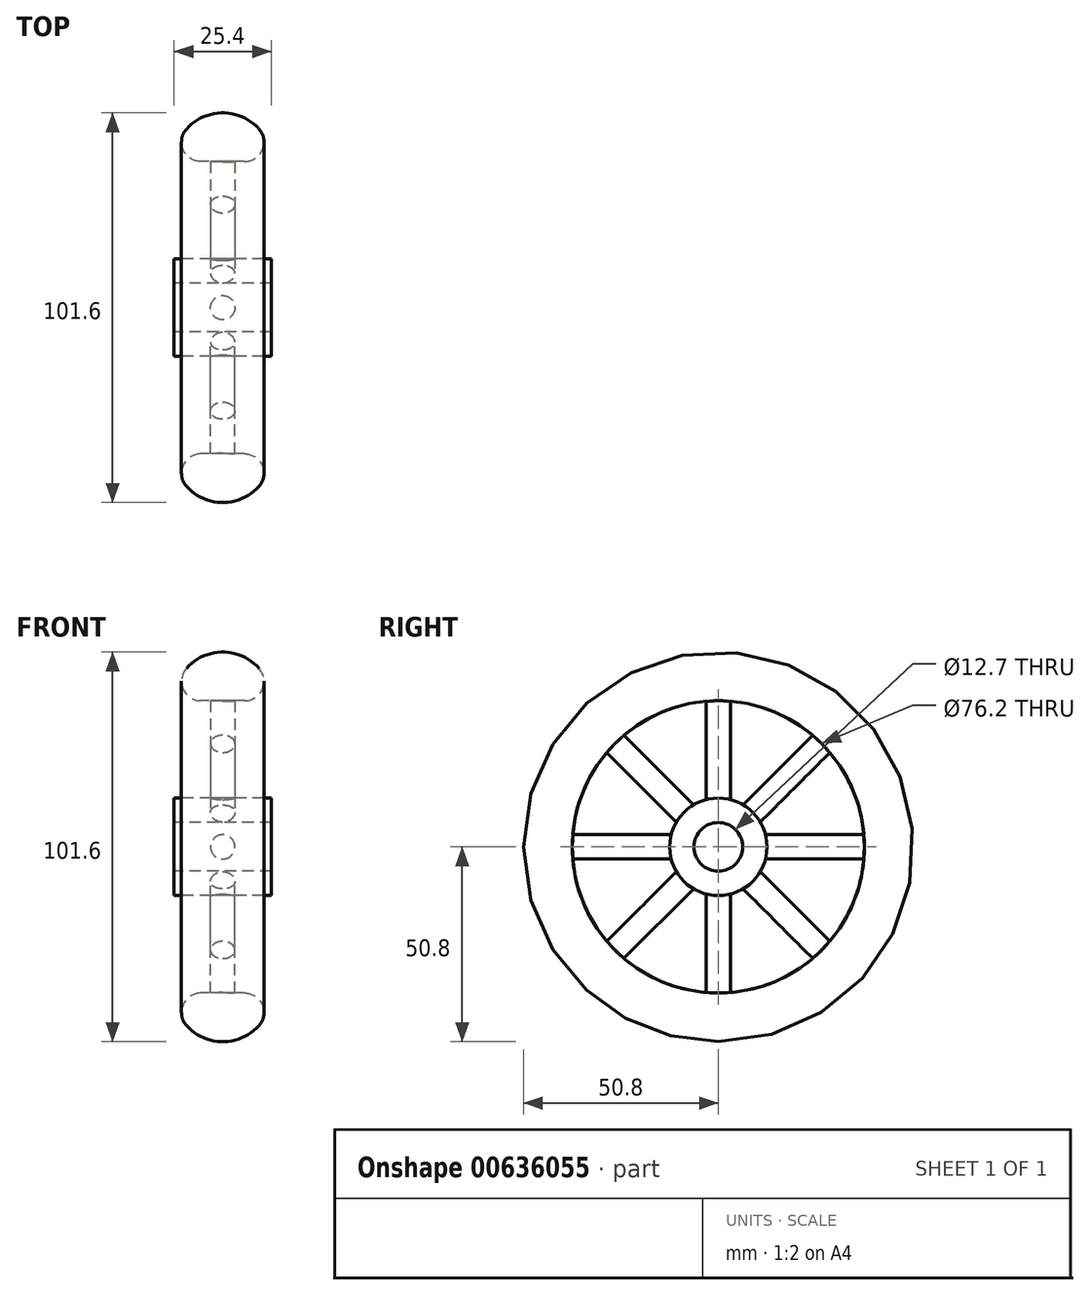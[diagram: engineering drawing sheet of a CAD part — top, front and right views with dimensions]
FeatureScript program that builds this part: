
annotation { "Feature Type Name" : "Feature", "Feature Type Description" : "" }
export const myFeature = defineFeature(function(context is Context, id is Id, definition is map)
    precondition{}
    {
        {
            var Q0;
            Q0=qCreatedBy(makeId("Right.planeOp"),FACE);
            var sketch = newSketch(context, id + "F0", { "sketchPlane" : qUnion([Q0])});
            skCircle(sketch, "E0", {"center": v(0, 0) * mm, "radius": 50.8 * mm});
            skCircle(sketch, "E1", {"center": v(0, 0) * mm, "radius": 38.1 * mm});
            skCircle(sketch, "E2", {"center": v(0, 0) * mm, "radius": 6.35 * mm});
            skCircle(sketch, "E3", {"center": v(0, 0) * mm, "radius": 12.7 * mm});
            skLineSegment(sketch, "E4.0", {"start": v(-3.18, 12.3) * mm, "end": v(-3.18, 37.97) * mm});
            skLineSegment(sketch, "E5.0", {"start": v(3.17, 12.3) * mm, "end": v(3.17, 37.97) * mm});
            skLineSegment(sketch, "E6.1.0", {"start": v(-10.94, 6.45) * mm, "end": v(-29.1, 24.6) * mm});
            skLineSegment(sketch, "E6.1.1", {"start": v(-6.45, 10.94) * mm, "end": v(-24.6, 29.1) * mm});
            skLineSegment(sketch, "E6.2.0", {"start": v(-12.3, -3.18) * mm, "end": v(-37.97, -3.17) * mm});
            skLineSegment(sketch, "E6.2.1", {"start": v(-12.3, 3.17) * mm, "end": v(-37.97, 3.18) * mm});
            skLineSegment(sketch, "E6.3.0", {"start": v(-6.45, -10.94) * mm, "end": v(-24.6, -29.1) * mm});
            skLineSegment(sketch, "E6.3.1", {"start": v(-10.94, -6.45) * mm, "end": v(-29.1, -24.6) * mm});
            skLineSegment(sketch, "E6.4.0", {"start": v(3.18, -12.3) * mm, "end": v(3.17, -37.97) * mm});
            skLineSegment(sketch, "E6.4.1", {"start": v(-3.18, -12.3) * mm, "end": v(-3.18, -37.97) * mm});
            skLineSegment(sketch, "E6.5.0", {"start": v(10.94, -6.45) * mm, "end": v(29.1, -24.6) * mm});
            skLineSegment(sketch, "E6.5.1", {"start": v(6.45, -10.94) * mm, "end": v(24.6, -29.1) * mm});
            skLineSegment(sketch, "E6.6.0", {"start": v(12.3, 3.18) * mm, "end": v(37.97, 3.17) * mm});
            skLineSegment(sketch, "E6.6.1", {"start": v(12.3, -3.18) * mm, "end": v(37.97, -3.18) * mm});
            skLineSegment(sketch, "E6.7.0", {"start": v(6.45, 10.94) * mm, "end": v(24.6, 29.1) * mm});
            skLineSegment(sketch, "E6.7.1", {"start": v(10.94, 6.45) * mm, "end": v(29.1, 24.6) * mm});
            skSolve(sketch);
        }
        {
            var Q0;
            Q0=makeQuery(id+"F0.imprint","IMPRINT",FACE,{"disambiguationData":[TD([[makeQuery(id+"F0.imprint","IMPRINT",EDGE,{"derivedFrom":sQuery(id+"F0.wireOp",EDGE,"E0")}),1.0]])]});
            extrude(context, id + "F1", {"entities" : qUnion([Q0]), "endBound" : BoundingType.SYMMETRIC, "depth" : 25.4 * mm, "offsetDistance" : 25.4 * mm});
        }
        {
            var Q0;
            Q0=makeQuery(id+"F0.imprint","IMPRINT",FACE,{"disambiguationData":[TD([[makeQuery(id+"F0.imprint","IMPRINT",EDGE,{"derivedFrom":sQuery(id+"F0.wireOp",EDGE,"E2")}),-1.0]])]});
            extrude(context, id + "F2", {"entities" : qUnion([Q0]), "endBound" : BoundingType.SYMMETRIC, "depth" : 25.4 * mm, "offsetDistance" : 25.4 * mm});
        }
        {
            var Q0;
            {var subQ0=sQuery(id+"F0.wireOp",EDGE,"E6.1.0");Q0=makeQuery(id+"F0.imprint","IMPRINT",FACE,{"disambiguationData":[TD([[makeQuery(id+"F0.imprint","IMPRINT",EDGE,{"derivedFrom":subQ0}),-1.0]])]});}
            var Q1;
            {var subQ0=sQuery(id+"F0.wireOp",EDGE,"E4.0");Q1=makeQuery(id+"F0.imprint","IMPRINT",FACE,{"disambiguationData":[TD([[makeQuery(id+"F0.imprint","IMPRINT",EDGE,{"derivedFrom":subQ0}),-1.0]])]});}
            var Q2;
            {var subQ0=sQuery(id+"F0.wireOp",EDGE,"E6.7.0");Q2=makeQuery(id+"F0.imprint","IMPRINT",FACE,{"disambiguationData":[TD([[makeQuery(id+"F0.imprint","IMPRINT",EDGE,{"derivedFrom":subQ0}),-1.0]])]});}
            var Q3;
            {var subQ0=sQuery(id+"F0.wireOp",EDGE,"E6.6.0");Q3=makeQuery(id+"F0.imprint","IMPRINT",FACE,{"disambiguationData":[TD([[makeQuery(id+"F0.imprint","IMPRINT",EDGE,{"derivedFrom":subQ0}),-1.0]])]});}
            var Q4;
            {var subQ0=sQuery(id+"F0.wireOp",EDGE,"E6.2.0");Q4=makeQuery(id+"F0.imprint","IMPRINT",FACE,{"disambiguationData":[TD([[makeQuery(id+"F0.imprint","IMPRINT",EDGE,{"derivedFrom":subQ0}),-1.0]])]});}
            var Q5;
            {var subQ0=sQuery(id+"F0.wireOp",EDGE,"E6.3.0");Q5=makeQuery(id+"F0.imprint","IMPRINT",FACE,{"disambiguationData":[TD([[makeQuery(id+"F0.imprint","IMPRINT",EDGE,{"derivedFrom":subQ0}),-1.0]])]});}
            var Q6;
            {var subQ0=sQuery(id+"F0.wireOp",EDGE,"E6.4.0");Q6=makeQuery(id+"F0.imprint","IMPRINT",FACE,{"disambiguationData":[TD([[makeQuery(id+"F0.imprint","IMPRINT",EDGE,{"derivedFrom":subQ0}),-1.0]])]});}
            var Q7;
            {var subQ0=sQuery(id+"F0.wireOp",EDGE,"E6.5.0");Q7=makeQuery(id+"F0.imprint","IMPRINT",FACE,{"disambiguationData":[TD([[makeQuery(id+"F0.imprint","IMPRINT",EDGE,{"derivedFrom":subQ0}),-1.0]])]});}
            extrude(context, id + "F3", {"entities" : qUnion([Q0, Q1, Q2, Q3, Q4, Q5, Q6, Q7]), "endBound" : BoundingType.SYMMETRIC, "depth" : 6.35 * mm, "offsetDistance" : 25.4 * mm});
        }
        {
            var Q0;
            Q0=makeQuery(id+"F1.opExtrude","CAP_EDGE",EDGE,{"disambiguationData":[OSD([sQuery(id+"F0.wireOp",EDGE,"E0")])],"isStart":false});
            var Q1;
            Q1=makeQuery(id+"F1.opExtrude","CAP_EDGE",EDGE,{"disambiguationData":[OSD([sQuery(id+"F0.wireOp",EDGE,"E0")])],"isStart":true});
            fillet(context, id + "F4", {"entities" : qUnion([Q0, Q1]), "radius" : 12.7 * mm, "tangentPropagation" : true, "allowEdgeOverflow" : false});
        }
        {
            var Q0;
            Q0=makeQuery(id+"F4.opFillet","BLEND_EDGE",EDGE,{"blendedFrom":[makeQuery(id+"F1.opExtrude","CAP_EDGE",EDGE,{"disambiguationData":[OSD([sQuery(id+"F0.wireOp",EDGE,"E0")])],"isStart":true}),makeQuery(id+"F1.opExtrude","SWEPT_FACE",FACE,{"disambiguationData":[OSD([sQuery(id+"F0.wireOp",EDGE,"E1")])]})],"blendedInto":[makeQuery(id+"F1.opExtrude","SWEPT_FACE",FACE,{"disambiguationData":[OSD([sQuery(id+"F0.wireOp",EDGE,"E1")])]})]});
            var Q1;
            Q1=makeQuery(id+"F4.opFillet","BLEND_EDGE",EDGE,{"blendedFrom":[makeQuery(id+"F1.opExtrude","CAP_EDGE",EDGE,{"disambiguationData":[OSD([sQuery(id+"F0.wireOp",EDGE,"E0")])],"isStart":false}),makeQuery(id+"F1.opExtrude","SWEPT_FACE",FACE,{"disambiguationData":[OSD([sQuery(id+"F0.wireOp",EDGE,"E1")])]})],"blendedInto":[makeQuery(id+"F1.opExtrude","SWEPT_FACE",FACE,{"disambiguationData":[OSD([sQuery(id+"F0.wireOp",EDGE,"E1")])]})]});
            fillet(context, id + "F5", {"entities" : qUnion([Q0, Q1]), "radius" : 5.08 * mm, "tangentPropagation" : true, "allowEdgeOverflow" : false});
        }
        {
            var Q0;
            Q0=makeQuery(id+"F3.opExtrude","CAP_EDGE",EDGE,{"disambiguationData":[OSD([sQuery(id+"F0.wireOp",EDGE,"E6.1.0")])],"isStart":false});
            var Q1;
            Q1=makeQuery(id+"F3.opExtrude","CAP_EDGE",EDGE,{"disambiguationData":[OSD([sQuery(id+"F0.wireOp",EDGE,"E4.0")])],"isStart":false});
            var Q2;
            Q2=makeQuery(id+"F3.opExtrude","CAP_EDGE",EDGE,{"disambiguationData":[OSD([sQuery(id+"F0.wireOp",EDGE,"E6.1.1")])],"isStart":false});
            var Q3;
            Q3=makeQuery(id+"F3.opExtrude","CAP_EDGE",EDGE,{"disambiguationData":[OSD([sQuery(id+"F0.wireOp",EDGE,"E5.0")])],"isStart":false});
            var Q4;
            Q4=makeQuery(id+"F3.opExtrude","CAP_EDGE",EDGE,{"disambiguationData":[OSD([sQuery(id+"F0.wireOp",EDGE,"E6.7.0")])],"isStart":false});
            var Q5;
            Q5=makeQuery(id+"F3.opExtrude","CAP_EDGE",EDGE,{"disambiguationData":[OSD([sQuery(id+"F0.wireOp",EDGE,"E6.7.1")])],"isStart":false});
            var Q6;
            Q6=makeQuery(id+"F3.opExtrude","CAP_EDGE",EDGE,{"disambiguationData":[OSD([sQuery(id+"F0.wireOp",EDGE,"E6.6.0")])],"isStart":false});
            var Q7;
            Q7=makeQuery(id+"F3.opExtrude","CAP_EDGE",EDGE,{"disambiguationData":[OSD([sQuery(id+"F0.wireOp",EDGE,"E6.6.1")])],"isStart":false});
            var Q8;
            Q8=makeQuery(id+"F3.opExtrude","CAP_EDGE",EDGE,{"disambiguationData":[OSD([sQuery(id+"F0.wireOp",EDGE,"E6.5.0")])],"isStart":false});
            var Q9;
            Q9=makeQuery(id+"F3.opExtrude","CAP_EDGE",EDGE,{"disambiguationData":[OSD([sQuery(id+"F0.wireOp",EDGE,"E6.5.1")])],"isStart":false});
            var Q10;
            Q10=makeQuery(id+"F3.opExtrude","CAP_EDGE",EDGE,{"disambiguationData":[OSD([sQuery(id+"F0.wireOp",EDGE,"E6.4.0")])],"isStart":false});
            var Q11;
            Q11=makeQuery(id+"F3.opExtrude","CAP_EDGE",EDGE,{"disambiguationData":[OSD([sQuery(id+"F0.wireOp",EDGE,"E6.4.1")])],"isStart":false});
            var Q12;
            Q12=makeQuery(id+"F3.opExtrude","CAP_EDGE",EDGE,{"disambiguationData":[OSD([sQuery(id+"F0.wireOp",EDGE,"E6.3.0")])],"isStart":false});
            var Q13;
            Q13=makeQuery(id+"F3.opExtrude","CAP_EDGE",EDGE,{"disambiguationData":[OSD([sQuery(id+"F0.wireOp",EDGE,"E6.3.1")])],"isStart":false});
            var Q14;
            Q14=makeQuery(id+"F3.opExtrude","CAP_EDGE",EDGE,{"disambiguationData":[OSD([sQuery(id+"F0.wireOp",EDGE,"E6.2.0")])],"isStart":false});
            var Q15;
            Q15=makeQuery(id+"F3.opExtrude","CAP_EDGE",EDGE,{"disambiguationData":[OSD([sQuery(id+"F0.wireOp",EDGE,"E6.2.1")])],"isStart":false});
            var Q16;
            Q16=makeQuery(id+"F3.opExtrude","CAP_EDGE",EDGE,{"disambiguationData":[OSD([sQuery(id+"F0.wireOp",EDGE,"E6.7.1")])],"isStart":true});
            var Q17;
            Q17=makeQuery(id+"F3.opExtrude","CAP_EDGE",EDGE,{"disambiguationData":[OSD([sQuery(id+"F0.wireOp",EDGE,"E6.7.0")])],"isStart":true});
            var Q18;
            Q18=makeQuery(id+"F3.opExtrude","CAP_EDGE",EDGE,{"disambiguationData":[OSD([sQuery(id+"F0.wireOp",EDGE,"E5.0")])],"isStart":true});
            var Q19;
            Q19=makeQuery(id+"F3.opExtrude","CAP_EDGE",EDGE,{"disambiguationData":[OSD([sQuery(id+"F0.wireOp",EDGE,"E4.0")])],"isStart":true});
            var Q20;
            Q20=makeQuery(id+"F3.opExtrude","CAP_EDGE",EDGE,{"disambiguationData":[OSD([sQuery(id+"F0.wireOp",EDGE,"E6.1.1")])],"isStart":true});
            var Q21;
            Q21=makeQuery(id+"F3.opExtrude","CAP_EDGE",EDGE,{"disambiguationData":[OSD([sQuery(id+"F0.wireOp",EDGE,"E6.1.0")])],"isStart":true});
            var Q22;
            Q22=makeQuery(id+"F3.opExtrude","CAP_EDGE",EDGE,{"disambiguationData":[OSD([sQuery(id+"F0.wireOp",EDGE,"E6.2.1")])],"isStart":true});
            var Q23;
            Q23=makeQuery(id+"F3.opExtrude","CAP_EDGE",EDGE,{"disambiguationData":[OSD([sQuery(id+"F0.wireOp",EDGE,"E6.2.0")])],"isStart":true});
            var Q24;
            Q24=makeQuery(id+"F3.opExtrude","CAP_EDGE",EDGE,{"disambiguationData":[OSD([sQuery(id+"F0.wireOp",EDGE,"E6.3.1")])],"isStart":true});
            var Q25;
            Q25=makeQuery(id+"F3.opExtrude","CAP_EDGE",EDGE,{"disambiguationData":[OSD([sQuery(id+"F0.wireOp",EDGE,"E6.3.0")])],"isStart":true});
            var Q26;
            Q26=makeQuery(id+"F3.opExtrude","CAP_EDGE",EDGE,{"disambiguationData":[OSD([sQuery(id+"F0.wireOp",EDGE,"E6.4.1")])],"isStart":true});
            var Q27;
            Q27=makeQuery(id+"F3.opExtrude","CAP_EDGE",EDGE,{"disambiguationData":[OSD([sQuery(id+"F0.wireOp",EDGE,"E6.4.0")])],"isStart":true});
            var Q28;
            Q28=makeQuery(id+"F3.opExtrude","CAP_EDGE",EDGE,{"disambiguationData":[OSD([sQuery(id+"F0.wireOp",EDGE,"E6.5.1")])],"isStart":true});
            var Q29;
            Q29=makeQuery(id+"F3.opExtrude","CAP_EDGE",EDGE,{"disambiguationData":[OSD([sQuery(id+"F0.wireOp",EDGE,"E6.5.0")])],"isStart":true});
            var Q30;
            Q30=makeQuery(id+"F3.opExtrude","CAP_EDGE",EDGE,{"disambiguationData":[OSD([sQuery(id+"F0.wireOp",EDGE,"E6.6.1")])],"isStart":true});
            var Q31;
            Q31=makeQuery(id+"F3.opExtrude","CAP_EDGE",EDGE,{"disambiguationData":[OSD([sQuery(id+"F0.wireOp",EDGE,"E6.6.0")])],"isStart":true});
            fillet(context, id + "F6", {"entities" : qUnion([Q0, Q1, Q2, Q3, Q4, Q5, Q6, Q7, Q8, Q9, Q10, Q11, Q12, Q13, Q14, Q15, Q16, Q17, Q18, Q19, Q20, Q21, Q22, Q23, Q24, Q25, Q26, Q27, Q28, Q29, Q30, Q31]), "radius" : 3.17 * mm, "tangentPropagation" : true, "allowEdgeOverflow" : false});
        }
    });
